# Revit family: OCR- Single
name_source: partatom
category: Lighting Fixtures
revit_build: Autodesk Revit MEP 2012 (Build: 20110916_2132(x64)
units: mm (PartAtom-declared; Revit-internal decimal feet)

## types (3) — shared parameters
Apparent Load = 5 VA
Default Elevation = 48.000"
Description = Outdoor diecast Aluminum Wet Location Listed Remote Lighting Heads
Lamp = Halogen MR16,LED
Load Classification = Lighting
Manufacturer = Dual-lite
Manufacturer Fax = 866-898-0131
Model = OCR- Single
Photometric Web = Web OCR : OCR Series with 3W LED Lamp
Product Documentation Link = http://cdn.dual-lite.com
Product Page URL = http://www.dual-lite.com
Total Input Wattage = 5 W
URL = http://www.dual-lite.com
Voltage = 120 V

## per-type parameters (varying)
| type | Material Finish | Tilt Angle | zz Angle1 |
| OCR Single- White | Hubbell-Aluminum- White | 45.00° | 45.00° |
| OCR Single - Black | Hubbell-Aluminum- Black | 45.00° | 45.00° |
| OCR Single - Dark Bronze | Hubbell-Aluminum-Dark Bronze | 70.00° | 70.00° |

## geometry (parser evidence)
native form markers: Blend x8, Sweep x7
no freeform markers — native parametric forms only
